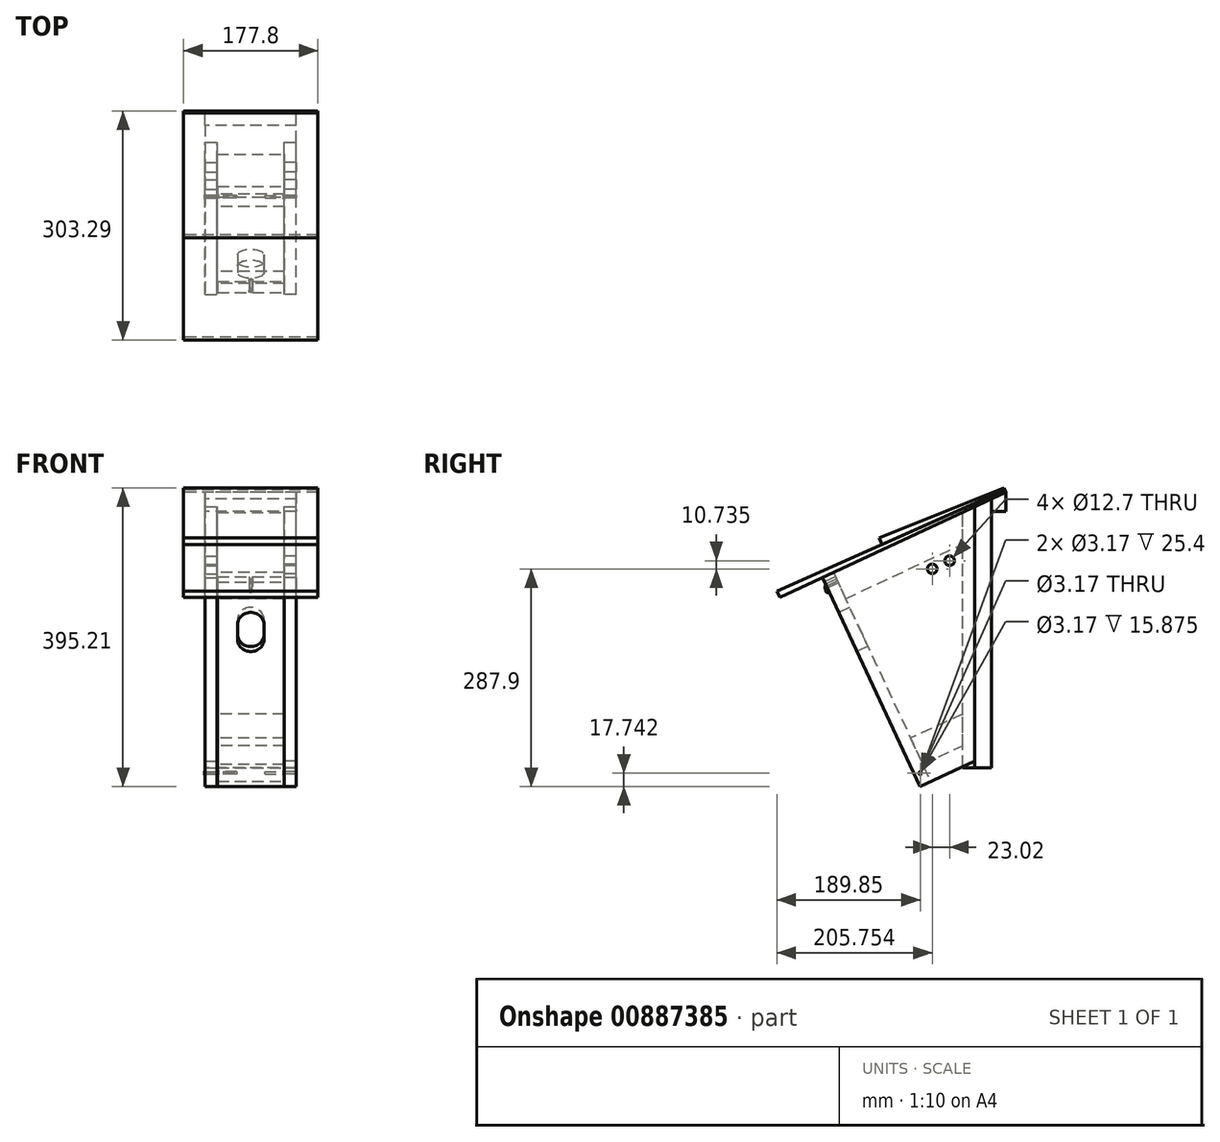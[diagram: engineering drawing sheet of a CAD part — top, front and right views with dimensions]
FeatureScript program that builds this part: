
annotation { "Feature Type Name" : "Feature", "Feature Type Description" : "" }
export const myFeature = defineFeature(function(context is Context, id is Id, definition is map)
    precondition{}
    {
        {
            var Q0;
            Q0=qCreatedBy(makeId("Top.planeOp"),FACE);
            var sketch = newSketch(context, id + "F0", { "sketchPlane" : qUnion([Q0])});
            skLineSegment(sketch, "E0", {"start": v(-60.33, 0) * mm, "end": v(-60.33, -22.23) * mm});
            skLineSegment(sketch, "E1", {"start": v(-60.32, -22.23) * mm, "end": v(-44.45, -22.23) * mm});
            skLineSegment(sketch, "E2", {"start": v(-44.45, -22.23) * mm, "end": v(-44.45, -38.1) * mm});
            skLineSegment(sketch, "E3", {"start": v(-44.45, -38.1) * mm, "end": v(44.45, -38.1) * mm});
            skLineSegment(sketch, "E4", {"start": v(44.45, -38.1) * mm, "end": v(44.45, -22.23) * mm});
            skLineSegment(sketch, "E5", {"start": v(44.45, -22.23) * mm, "end": v(60.32, -22.23) * mm});
            skLineSegment(sketch, "E6", {"start": v(60.33, -22.23) * mm, "end": v(60.33, 0) * mm});
            skLineSegment(sketch, "E7", {"start": v(60.33, 0) * mm, "end": v(-60.33, 0) * mm});
            skSolve(sketch);
        }
        {
            var Q0;
            Q0 = qSketchRegion(id + "F0", true);
            extrude(context, id + "F1", {"entities" : qUnion([Q0]), "oppositeDirection" : true, "depth" : 355.6 * mm, "offsetDistance" : 25.4 * mm});
        }
        {
            var Q0;
            Q0=qCreatedBy(makeId("Right.planeOp"),FACE);
            var sketch = newSketch(context, id + "F2", { "sketchPlane" : qUnion([Q0])});
            skLineSegment(sketch, "E8", {"start": v(0, 0) * mm, "end": v(-38.1, 0) * mm});
            skLineSegment(sketch, "E9", {"start": v(-38.1, 0) * mm, "end": v(-38.1, -17.77) * mm});
            skLineSegment(sketch, "E10", {"start": v(-38.1, -17.77) * mm, "end": v(0, 0) * mm});
            skSolve(sketch);
        }
        {
            var Q0;
            Q0 = qSketchRegion(id + "F2", true);
            extrude(context, id + "F3", {"entities" : qUnion([Q0]), "operationType" : NewBodyOperationType.REMOVE, "endBound" : BoundingType.THROUGH_ALL, "oppositeDirection" : true, "depth" : 25.4 * mm, "offsetDistance" : 25.4 * mm, "hasSecondDirection" : true, "secondDirectionBound" : SecondDirectionBoundingType.THROUGH_ALL, "secondDirectionOppositeDirection" : false, "secondDirectionDepth" : 25.4 * mm});
        }
        {
            var Q0;
            Q0=qCreatedBy(makeId("Right.planeOp"),FACE);
            var sketch = newSketch(context, id + "F4", { "sketchPlane" : qUnion([Q0])});
            skLineSegment(sketch, "E11", {"start": v(-38.1, -17.77) * mm, "end": v(-209.3, -97.6) * mm});
            skLineSegment(sketch, "E12", {"start": v(-209.3, -97.6) * mm, "end": v(-193.2, -132.13) * mm});
            skLineSegment(sketch, "E13", {"start": v(-193.2, -132.13) * mm, "end": v(-38.1, -59.8) * mm});
            skLineSegment(sketch, "E14", {"start": v(-38.1, -59.8) * mm, "end": v(-38.1, -17.77) * mm});
            skSolve(sketch);
        }
        {
            var Q0;
            Q0 = qSketchRegion(id + "F4", true);
            extrude(context, id + "F5", {"entities" : qUnion([Q0]), "endBound" : BoundingType.SYMMETRIC, "depth" : 88.9 * mm, "offsetDistance" : 25.4 * mm});
        }
        {
            var Q0;
            Q0=qCreatedBy(makeId("Right.planeOp"),FACE);
            var sketch = newSketch(context, id + "F6", { "sketchPlane" : qUnion([Q0])});
            skLineSegment(sketch, "E15", {"start": v(-38.1, -284.47) * mm, "end": v(-107.15, -316.66) * mm});
            skLineSegment(sketch, "E16", {"start": v(-107.15, -316.66) * mm, "end": v(-91.05, -351.2) * mm});
            skLineSegment(sketch, "E17", {"start": v(-91.05, -351.2) * mm, "end": v(-38.1, -326.5) * mm});
            skLineSegment(sketch, "E18", {"start": v(-38.1, -326.5) * mm, "end": v(-38.1, -284.47) * mm});
            skSolve(sketch);
        }
        {
            var Q0;
            Q0 = qSketchRegion(id + "F6", true);
            extrude(context, id + "F7", {"entities" : qUnion([Q0]), "endBound" : BoundingType.SYMMETRIC, "depth" : 88.9 * mm, "offsetDistance" : 25.4 * mm});
        }
        {
            var Q0;
            Q0=makeQuery(id+"F1.opExtrude","SWEPT_FACE",FACE,{"disambiguationData":[OSD([sQuery(id+"F0.wireOp",EDGE,"E2")])]});
            var sketch = newSketch(context, id + "F8", { "sketchPlane" : qUnion([Q0])});
            skLineSegment(sketch, "E19", {"start": v(22.22, -10.36) * mm, "end": v(223.69, -104.3) * mm});
            skLineSegment(sketch, "E20", {"start": v(223.69, -104.3) * mm, "end": v(94.87, -380.55) * mm});
            skLineSegment(sketch, "E21", {"start": v(94.87, -380.55) * mm, "end": v(22.23, -346.67) * mm});
            skLineSegment(sketch, "E22", {"start": v(22.23, -346.67) * mm, "end": v(22.22, -10.36) * mm});
            skLineSegment(sketch, "E23", {"start": v(38.1, -73.82) * mm, "end": v(202.22, -150.35) * mm, "construction": true});
            skCircle(sketch, "E24", {"center": v(55.47, -81.92) * mm, "radius": 6.35 * mm});
            skCircle(sketch, "E25", {"center": v(78.49, -92.65) * mm, "radius": 6.35 * mm});
            skCircle(sketch, "E26", {"center": v(94.4, -362.8) * mm, "radius": 1.59 * mm});
            skSolve(sketch);
        }
        {
            var Q0;
            Q0 = qSketchRegion(id + "F8", true);
            var Q1;
            Q1=makeQuery(id+"F1.opExtrude","SWEPT_FACE",FACE,{"disambiguationData":[OSD([sQuery(id+"F0.wireOp",EDGE,"E0")])]});
            extrude(context, id + "F9", {"entities" : qUnion([Q0]), "endBound" : BoundingType.UP_TO_SURFACE, "depth" : 25.4 * mm, "endBoundEntityFace" : qUnion([Q1]), "offsetDistance" : 25.4 * mm});
        }
        {
            var Q0;
            Q0=makeQuery(id+"F1.opExtrude","SWEPT_FACE",FACE,{"disambiguationData":[OSD([sQuery(id+"F0.wireOp",EDGE,"E4")])]});
            var sketch = newSketch(context, id + "F10", { "sketchPlane" : qUnion([Q0])});
            skLineSegment(sketch, "E27.0", {"start": v(-22.23, -10.36) * mm, "end": v(-223.69, -104.3) * mm});
            skLineSegment(sketch, "E27.1", {"start": v(-223.69, -104.3) * mm, "end": v(-94.87, -380.55) * mm});
            skLineSegment(sketch, "E27.2", {"start": v(-94.87, -380.55) * mm, "end": v(-22.23, -346.67) * mm});
            skLineSegment(sketch, "E27.3.0", {"start": v(-22.23, -346.67) * mm, "end": v(-94.87, -380.55) * mm});
            skLineSegment(sketch, "E27.3.1", {"start": v(-94.87, -380.55) * mm, "end": v(-223.69, -104.3) * mm});
            skLineSegment(sketch, "E27.3.2", {"start": v(-223.69, -104.3) * mm, "end": v(-22.22, -10.36) * mm});
            skLineSegment(sketch, "E27.3.3", {"start": v(-22.23, -10.36) * mm, "end": v(-22.23, -346.67) * mm});
            skCircle(sketch, "E28.0", {"center": v(-78.49, -92.65) * mm, "radius": 6.35 * mm});
            skCircle(sketch, "E28.1", {"center": v(-55.47, -81.92) * mm, "radius": 6.35 * mm});
            skCircle(sketch, "E29.0", {"center": v(-94.4, -362.8) * mm, "radius": 1.59 * mm});
            skSolve(sketch);
        }
        {
            var Q0;
            Q0 = qSketchRegion(id + "F10", true);
            var Q1;
            Q1=makeQuery(id+"F1.opExtrude","SWEPT_FACE",FACE,{"disambiguationData":[OSD([sQuery(id+"F0.wireOp",EDGE,"E6")])]});
            extrude(context, id + "F11", {"entities" : qUnion([Q0]), "endBound" : BoundingType.UP_TO_SURFACE, "depth" : 25.4 * mm, "endBoundEntityFace" : qUnion([Q1]), "offsetDistance" : 25.4 * mm});
        }
        {
            var Q0;
            Q0=makeQuery(id+"F9.opExtrude","SWEPT_FACE",FACE,{"disambiguationData":[OSD([sQuery(id+"F8.wireOp",EDGE,"E20")])]});
            var sketch = newSketch(context, id + "F12", { "sketchPlane" : qUnion([Q0])});
            skLineSegment(sketch, "E30.bottom", {"start": v(-44.04, -6.35) * mm, "end": v(-2.38, -6.35) * mm});
            skLineSegment(sketch, "E30.top", {"start": v(-44.04, -304.8) * mm, "end": v(44.04, -304.8) * mm});
            skLineSegment(sketch, "E30.left", {"start": v(-44.04, -6.35) * mm, "end": v(-44.04, -304.8) * mm});
            skLineSegment(sketch, "E30.right", {"start": v(44.04, -6.35) * mm, "end": v(44.04, -304.8) * mm});
            skLineSegment(sketch, "E31", {"start": v(0, -6.35) * mm, "end": v(0, -304.8) * mm, "construction": true});
            skLineSegment(sketch, "E32", {"start": v(-17.46, -90.49) * mm, "end": v(-17.46, -68.26) * mm});
            skArc(sketch, "E33", {"start": v(17.46, -68.26) * mm, "mid": v(0, -50.8) * mm, "end": v(-17.46, -68.26) * mm});
            skLineSegment(sketch, "E34", {"start": v(17.46, -68.26) * mm, "end": v(17.46, -90.49) * mm});
            skArc(sketch, "E35", {"start": v(-17.46, -90.49) * mm, "mid": v(0, -107.95) * mm, "end": v(17.46, -90.49) * mm});
            skLineSegment(sketch, "E36", {"start": v(-2.38, -6.35) * mm, "end": v(-2.38, -12.7) * mm});
            skArc(sketch, "E37", {"start": v(-2.38, -12.7) * mm, "mid": v(0, -15.08) * mm, "end": v(2.38, -12.7) * mm});
            skLineSegment(sketch, "E38", {"start": v(2.38, -12.7) * mm, "end": v(2.38, -6.35) * mm});
            skLineSegment(sketch, "E39.trimOffspring", {"start": v(2.38, -6.35) * mm, "end": v(44.04, -6.35) * mm});
            skSolve(sketch);
        }
        {
            var Q0;
            Q0 = qSketchRegion(id + "F12", true);
            extrude(context, id + "F13", {"entities" : qUnion([Q0]), "oppositeDirection" : true, "depth" : 15.88 * mm, "offsetDistance" : 25.4 * mm});
        }
        {
            var Q0;
            Q0=makeQuery(id+"F13.opExtrude","SWEPT_FACE",FACE,{"disambiguationData":[OSD([sQuery(id+"F12.wireOp",EDGE,"E30.left")])]});
            var sketch = newSketch(context, id + "F14", { "sketchPlane" : qUnion([Q0])});
            skCircle(sketch, "E40.0", {"center": v(94.4, -362.8) * mm, "radius": 1.59 * mm});
            skSolve(sketch);
        }
        {
            var Q0;
            Q0 = qSketchRegion(id + "F14", true);
            extrude(context, id + "F15", {"entities" : qUnion([Q0]), "operationType" : NewBodyOperationType.REMOVE, "oppositeDirection" : true, "depth" : 25.4 * mm, "offsetDistance" : 25.4 * mm});
        }
        {
            var Q0;
            Q0=makeQuery(id+"F13.opExtrude","SWEPT_FACE",FACE,{"disambiguationData":[OSD([sQuery(id+"F12.wireOp",EDGE,"E30.right")])]});
            var sketch = newSketch(context, id + "F16", { "sketchPlane" : qUnion([Q0])});
            skCircle(sketch, "E41.0", {"center": v(-94.4, -362.8) * mm, "radius": 1.59 * mm});
            skSolve(sketch);
        }
        {
            var Q0;
            Q0 = qSketchRegion(id + "F16", true);
            extrude(context, id + "F17", {"entities" : qUnion([Q0]), "operationType" : NewBodyOperationType.REMOVE, "oppositeDirection" : true, "depth" : 25.4 * mm, "offsetDistance" : 25.4 * mm});
        }
        {
            var Q0;
            Q0=qCreatedBy(makeId("Right.planeOp"),FACE);
            var sketch = newSketch(context, id + "F18", { "sketchPlane" : qUnion([Q0])});
            skLineSegment(sketch, "E42", {"start": v(-280.21, -130.67) * mm, "end": v(19.05, 8.88) * mm});
            skLineSegment(sketch, "E43", {"start": v(19.05, 8.88) * mm, "end": v(17.7, 11.76) * mm});
            skLineSegment(sketch, "E44", {"start": v(17.7, 11.76) * mm, "end": v(-284.24, -122.03) * mm});
            skLineSegment(sketch, "E45", {"start": v(-284.24, -122.03) * mm, "end": v(-280.21, -130.67) * mm});
            skSolve(sketch);
        }
        {
            var Q0;
            Q0 = qSketchRegion(id + "F18", true);
            extrude(context, id + "F19", {"entities" : qUnion([Q0]), "endBound" : BoundingType.SYMMETRIC, "depth" : 177.8 * mm, "offsetDistance" : 25.4 * mm});
        }
        {
            var Q0;
            Q0=qCreatedBy(makeId("Right.planeOp"),FACE);
            var sketch = newSketch(context, id + "F20", { "sketchPlane" : qUnion([Q0])});
            skLineSegment(sketch, "E46", {"start": v(17.7, 11.76) * mm, "end": v(-144.85, -60.27) * mm});
            skLineSegment(sketch, "E47", {"start": v(-144.85, -60.27) * mm, "end": v(-148.7, -51.56) * mm});
            skLineSegment(sketch, "E48", {"start": v(-148.7, -51.56) * mm, "end": v(16.42, 14.66) * mm});
            skLineSegment(sketch, "E49", {"start": v(16.42, 14.66) * mm, "end": v(17.7, 11.76) * mm});
            skSolve(sketch);
        }
        {
            var Q0;
            Q0 = qSketchRegion(id + "F20", true);
            var Q1;
            Q1=makeQuery(id+"F19.opExtrude","CAP_FACE",FACE,{"disambiguationData":[OSD([sQuery(id+"F18.wireOp",EDGE,"E42"),sQuery(id+"F18.wireOp",EDGE,"E43"),sQuery(id+"F18.wireOp",EDGE,"E44"),sQuery(id+"F18.wireOp",EDGE,"E45")])],"isStart":false});
            var Q2;
            Q2=makeQuery(id+"F19.opExtrude","CAP_FACE",FACE,{"disambiguationData":[OSD([sQuery(id+"F18.wireOp",EDGE,"E42"),sQuery(id+"F18.wireOp",EDGE,"E43"),sQuery(id+"F18.wireOp",EDGE,"E44"),sQuery(id+"F18.wireOp",EDGE,"E45")])],"isStart":true});
            extrude(context, id + "F21", {"entities" : qUnion([Q0]), "endBound" : BoundingType.UP_TO_SURFACE, "depth" : 25.4 * mm, "endBoundEntityFace" : qUnion([Q1]), "offsetDistance" : 25.4 * mm, "hasSecondDirection" : true, "secondDirectionBound" : SecondDirectionBoundingType.UP_TO_SURFACE, "secondDirectionOppositeDirection" : true, "secondDirectionDepth" : 25.4 * mm, "secondDirectionBoundEntityFace" : qUnion([Q2])});
        }
        {
            var Q0;
            Q0=qCreatedBy(makeId("Right.planeOp"),FACE);
            var sketch = newSketch(context, id + "F22", { "sketchPlane" : qUnion([Q0])});
            skLineSegment(sketch, "E50", {"start": v(0, 0) * mm, "end": v(19.05, 8.88) * mm});
            skLineSegment(sketch, "E51", {"start": v(19.05, 8.88) * mm, "end": v(19.05, -16.52) * mm});
            skLineSegment(sketch, "E52", {"start": v(19.05, -16.52) * mm, "end": v(0, -16.52) * mm});
            skLineSegment(sketch, "E53", {"start": v(0, -16.52) * mm, "end": v(0, 0) * mm});
            skSolve(sketch);
        }
        {
            var Q0;
            Q0 = qSketchRegion(id + "F22", true);
            extrude(context, id + "F23", {"entities" : qUnion([Q0]), "endBound" : BoundingType.SYMMETRIC, "depth" : 120.65 * mm, "offsetDistance" : 25.4 * mm});
        }
        {
            var Q0;
            Q0=makeQuery(id+"F9.opExtrude","CAP_FACE",FACE,{"disambiguationData":[OSD([sQuery(id+"F8.wireOp",EDGE,"E19"),sQuery(id+"F8.wireOp",EDGE,"E20"),sQuery(id+"F8.wireOp",EDGE,"E21"),sQuery(id+"F8.wireOp",EDGE,"E22"),sQuery(id+"F8.wireOp",EDGE,"E24"),sQuery(id+"F8.wireOp",EDGE,"E25"),sQuery(id+"F8.wireOp",EDGE,"E26")])],"isStart":false});
            var sketch = newSketch(context, id + "F24", { "sketchPlane" : qUnion([Q0])});
            skCircle(sketch, "E54", {"center": v(94.4, -362.8) * mm, "radius": 1.35 * mm});
            skSolve(sketch);
        }
        {
            var Q0;
            Q0 = qSketchRegion(id + "F24", true);
            extrude(context, id + "F25", {"entities" : qUnion([Q0]), "oppositeDirection" : true, "depth" : 38.1 * mm, "offsetDistance" : 25.4 * mm});
        }
        {
            var Q0;
            Q0=makeQuery(id+"F25.opExtrude","CAP_FACE",FACE,{"disambiguationData":[OSD([sQuery(id+"F24.wireOp",EDGE,"E54")])],"isStart":true});
            var sketch = newSketch(context, id + "F26", { "sketchPlane" : qUnion([Q0])});
            skCircle(sketch, "E55", {"center": v(94.4, -362.8) * mm, "radius": 2.7 * mm});
            skSolve(sketch);
        }
        {
            var Q0;
            Q0 = qSketchRegion(id + "F26", true);
            extrude(context, id + "F27", {"entities" : qUnion([Q0]), "operationType" : NewBodyOperationType.ADD, "depth" : 0.76 * mm, "offsetDistance" : 25.4 * mm});
        }
        {
            var Q0;
            Q0=qCreatedBy(makeId("Right.planeOp"),FACE);
            var sketch = newSketch(context, id + "F28", { "sketchPlane" : qUnion([Q0])});
            skLineSegment(sketch, "E56", {"start": v(-204.6, -107.67) * mm, "end": v(-216.12, -113.04) * mm});
            skLineSegment(sketch, "E57", {"start": v(-218.42, -119.37) * mm, "end": v(-216.4, -123.68) * mm});
            skPoint(sketch, "E58.visualSharp", {"position": v(-220.43, -115.05) * mm});
            skArc(sketch, "E58.filletArc", {"start": v(-216.12, -113.04) * mm, "mid": v(-218.58, -115.72) * mm, "end": v(-218.42, -119.37) * mm});
            skSolve(sketch);
        }
        {
            var Q0;
            Q0=makeQuery(id+"F5.opExtrude","SWEPT_FACE",FACE,{"disambiguationData":[OSD([sQuery(id+"F4.wireOp",EDGE,"E12")])]});
            var sketch = newSketch(context, id + "F29", { "sketchPlane" : qUnion([Q0])});
            skCircle(sketch, "E59", {"center": v(0, -11.11) * mm, "radius": 1.59 * mm});
            skSolve(sketch);
        }
        {
            var Q0;
            Q0 = qSketchRegion(id + "F29", true);
            var Q1;
            Q1 = qConstructionFilter(qBodyType(qCreatedBy(id + "F28" ,EDGE), BodyType.WIRE), ConstructionObject.NO);
            sweep(context, id + "F30", {"profiles" : qUnion([Q0]), "path" : qUnion([Q1])});
        }
        {
            var Q0;
            Q0=makeQuery(id+"F30.opSweep","CAP_EDGE",EDGE,{"disambiguationData":[OSD([sQuery(id+"F28.wireOp",VERTEX,"E57.end"),sQuery(id+"F29.wireOp",EDGE,"E59")])],"isStart":false});
            fillet(context, id + "F31", {"entities" : qUnion([Q0]), "radius" : 0.76 * mm, "tangentPropagation" : true, "allowEdgeOverflow" : false});
        }
    });
